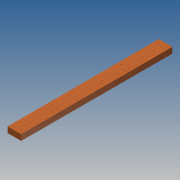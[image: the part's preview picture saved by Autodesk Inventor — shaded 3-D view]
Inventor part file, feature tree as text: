
AUTODESK INVENTOR PART (.ipt)
format: ipt  version: 2014 SP1 (Build 180222100, 222)  size: 121,344 bytes
history: native  units: in
note: dims shown in document units (in); Inventor stores cm internally (conversion verified against a paired STEP export)
features: sketch x5, hole x4, extrude x1
ambient origin geometry x8: Origin, YZ Plane, XZ Plane, XY Plane, X Axis, Y Axis, Z Axis, Center Point
bodies: Solid1 (feature_tree)
feature tree (10):
  extrude  "Extrusion1"  Depth=1.5in
  hole  "Hole1"  [1 undecoded]
  hole  "Hole2"  [1 undecoded]
  hole  "Hole3"  [1 undecoded]
  hole  "Hole4"  [1 undecoded]
  sketch  "Sketch1"  dims[d0=3.5in d1=1.5in]
  sketch  "Sketch2"  dims[d2=39.0in d3=0.0in d4=0.75in]
  sketch  "Sketch3"  dims[d5=0.75in d6=0.7874in d8=2.0in d9=0.7874in d11=37.5in]
  sketch  "Sketch4"  dims[d14=0.201in d15=0.75in d16=0.385in d17=0.25in d18=0.5635in d19=1.0in d20=0.8108in d21=9.0in]
  sketch  "Sketch5"  dims[d22=0.7874in d24=2.0in d25=0.3937in d27=1.0in d29=0.201in d30=0.75in d31=0.385in d32=0.25in d33=0.5635in d34=1.0in d35=0.8108in d36=8.25in d37=0.5in d38=0.201in d39=0.75in d40=0.385in d41=0.25in d42=0.5635in d43=1.0in d44=0.8108in d45=0.1in d46=0.75in d47=0.375in d48=0.25in d49=0.5635in d50=1.0in d51=0.8108in]
note: 4 required parameter values undecoded (feature->parameter linkage not recoverable at this tier; creation-order binding heuristic only, values carry confidence <= 0.55)
